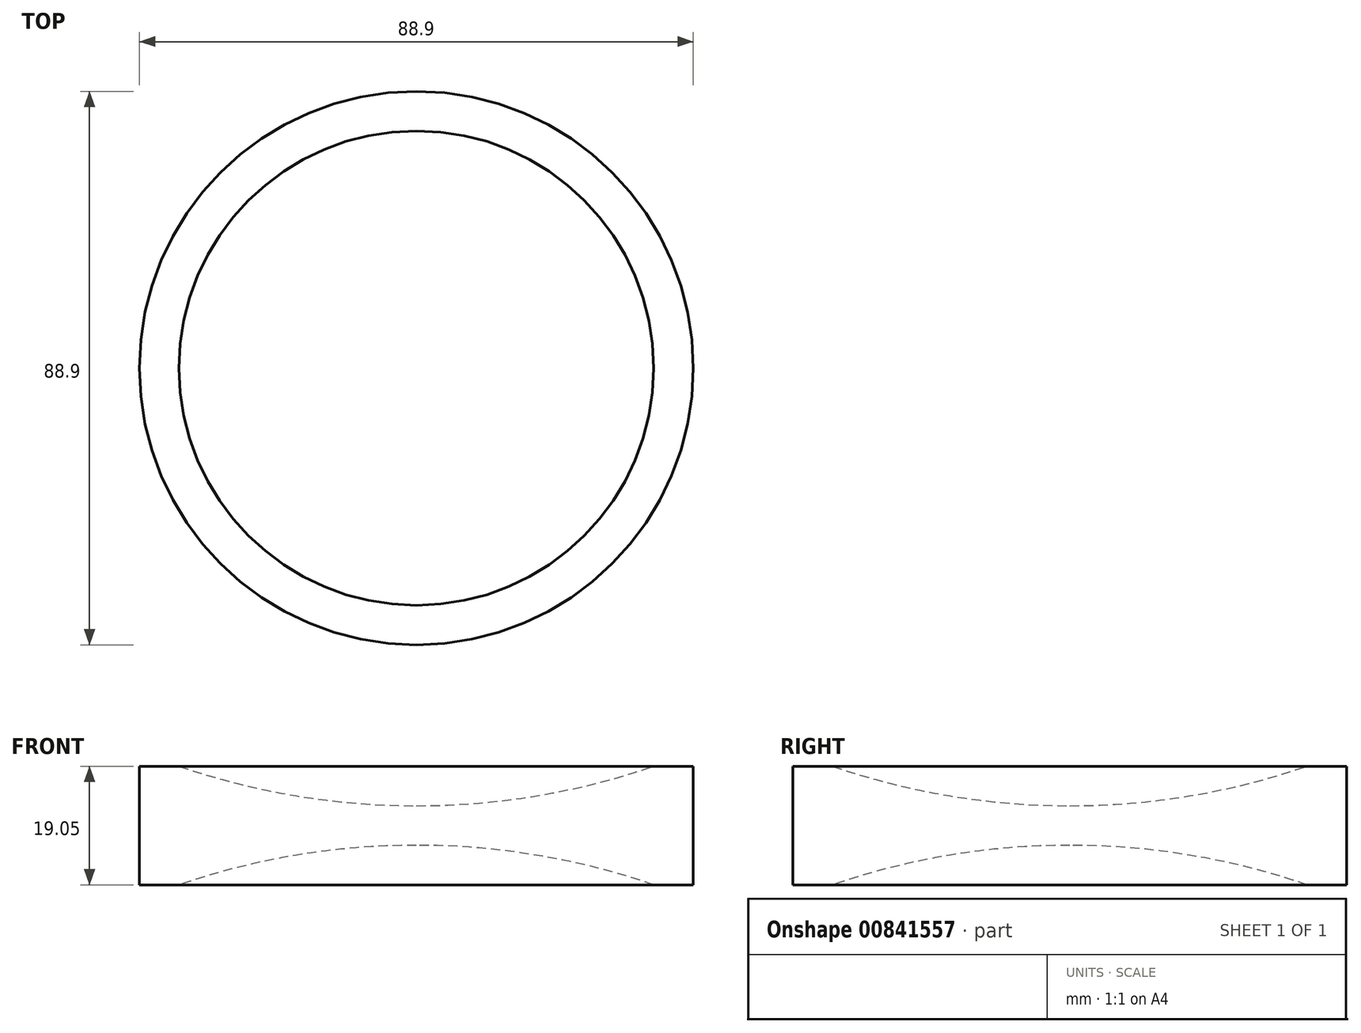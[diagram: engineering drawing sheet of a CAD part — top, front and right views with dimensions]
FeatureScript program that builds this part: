
annotation { "Feature Type Name" : "Feature", "Feature Type Description" : "" }
export const myFeature = defineFeature(function(context is Context, id is Id, definition is map)
    precondition{}
    {
        {
            var Q0;
            Q0=qCreatedBy(makeId("Front.planeOp"),FACE);
            var sketch = newSketch(context, id + "F0", { "sketchPlane" : qUnion([Q0])});
            skLineSegment(sketch, "E0.0", {"start": v(0, 6.35) * mm, "end": v(38.1, 6.35) * mm});
            skLineSegment(sketch, "E1.0", {"start": v(0, -12.7) * mm, "end": v(38.1, -12.7) * mm});
            skArc(sketch, "E2", {"start": v(0, 0) * mm, "mid": v(19.31, 1.6) * mm, "end": v(38.1, 6.35) * mm});
            skArc(sketch, "E3", {"start": v(38.1, -12.7) * mm, "mid": v(19.31, -7.95) * mm, "end": v(0, -6.35) * mm});
            skLineSegment(sketch, "E4", {"start": v(38.1, 6.35) * mm, "end": v(38.1, -12.7) * mm});
            skLineSegment(sketch, "E5", {"start": v(0, 0) * mm, "end": v(0, -6.35) * mm});
            skLineSegment(sketch, "E6.0", {"start": v(44.45, 6.35) * mm, "end": v(44.45, -12.7) * mm});
            skLineSegment(sketch, "E7", {"start": v(44.45, -12.7) * mm, "end": v(38.1, -12.7) * mm});
            skLineSegment(sketch, "E8", {"start": v(44.45, 6.35) * mm, "end": v(38.1, 6.35) * mm});
            skSolve(sketch);
        }
        {
            var Q0;
            Q0 = qSketchRegion(id + "F0", true);
            var Q1;
            Q1=sQuery(id+"F0.wireOp",EDGE,"E5");
            revolve(context, id + "F1", {"surfaceOperationType" : NewSurfaceOperationType.NEW, "entities" : qUnion([Q0]), "axis" : qUnion([Q1]), "revolveType" : RevolveType.FULL});
        }
    });
